# Revit family: Sink-Under_Mount-Lavatory-KOHLER-Kathryn-K-14275
name_source: partatom
category: Plumbing Fixtures
revit_build: Autodesk Revit 2015 (Build: 20140606_1530(x64)
units: mm (PartAtom-declared; Revit-internal decimal feet)

## types (3) — shared parameters
ADA Compliant = Yes
Assembly Code = D2010400
CW Connection = No
Cold Water Inlet = Cold Water Inlet
Date Modified = 10/23/2019
Default Elevation = 34"
Description = Under-mount bathroom sink
Drain Included = No
Finish = Kohler-Vitreous_China-0-White
HW Connection = No
Height = 6 3/4"
Hot Water Inlet = Hot Water Inlet
Length = 19 3/4"
Manufacturer = KOHLER Co.
MasterFormat 1995 = 15410
MasterFormat 2004 = 22.41.16
Material = Vitreous China
Product Documentation Link = https://www.us.kohler.com
Product Page URL = http://www.us.kohler.com
URL = https://www.us.kohler.com
Vent Connection = No
Waste Connection = Yes
Waste Water Outlet = Waste Water Outlet
WaterSense Certified = No
Width = 15 5/8"

## per-type parameters (varying)
| type | Model | Product Name | Type |
| Empress Bouquet, 0-White | K-14275-SMC-0 | Empress Bouquet Kathryn | 1 |
| Imperial Blue, 0-White | K-14275-VB-0 | Imperial Blue Kathryn | 2 |
| Botanical Study, 0-White | K-14275-BT-0 | Botanical Study Kathryn | 3 |

## geometry (parser evidence)
native form markers: Sweep x5
no freeform markers — native parametric forms only
